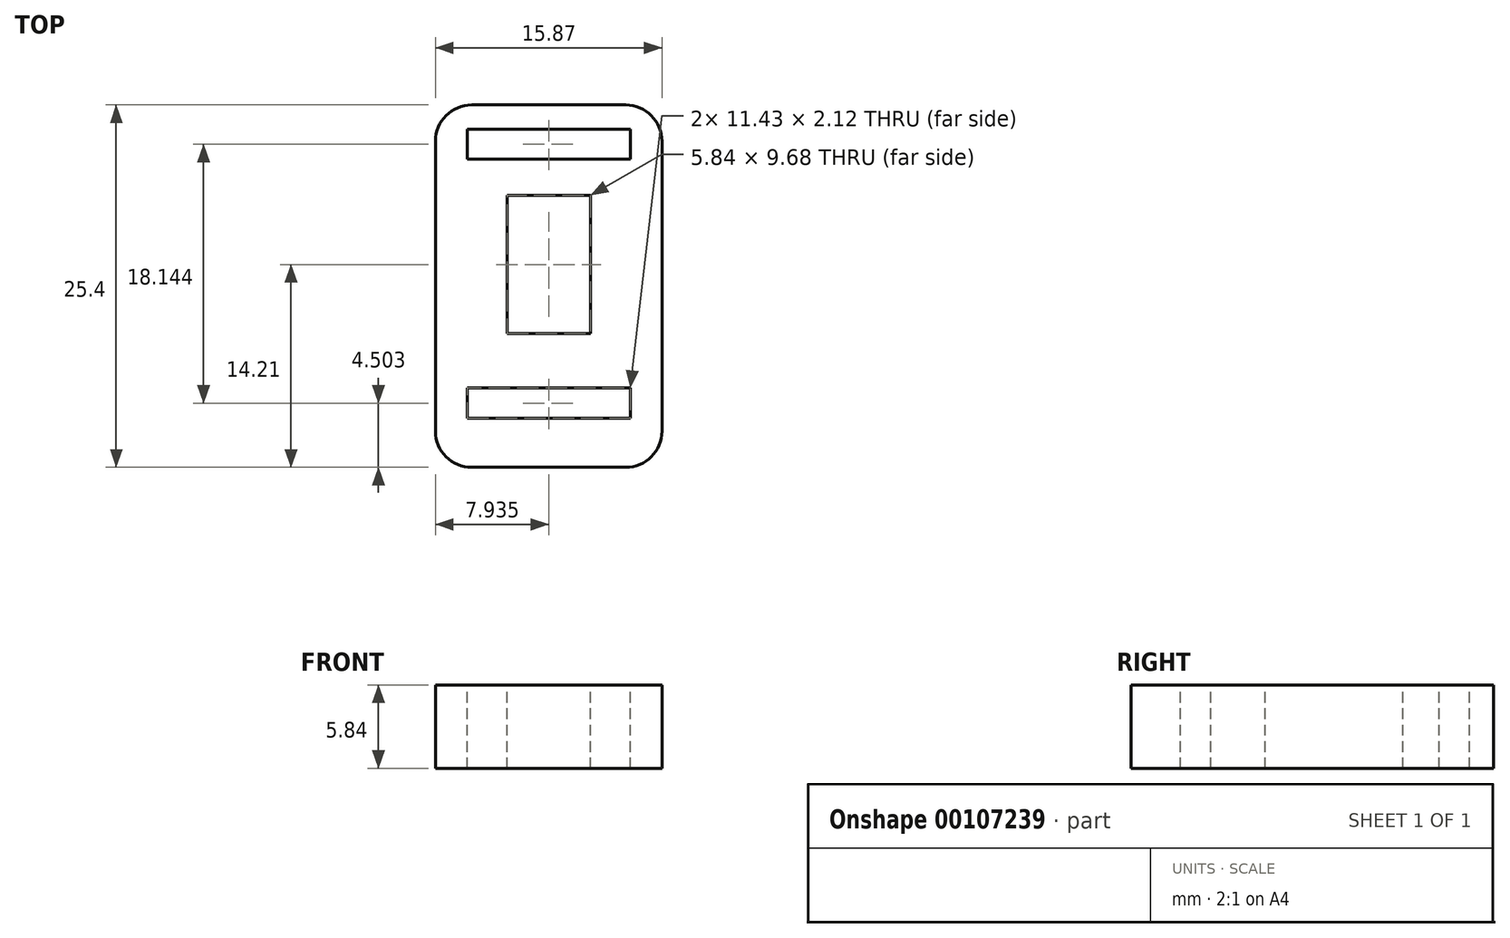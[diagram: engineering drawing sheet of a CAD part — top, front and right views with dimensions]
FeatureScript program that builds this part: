
annotation { "Feature Type Name" : "Feature", "Feature Type Description" : "" }
export const myFeature = defineFeature(function(context is Context, id is Id, definition is map)
    precondition{}
    {
        {
            var Q0;
            Q0=qCreatedBy(makeId("Top.planeOp"),FACE);
            var sketch = newSketch(context, id + "F0", { "sketchPlane" : qUnion([Q0])});
            skLineSegment(sketch, "E0.bottom", {"start": v(-6.16, -11.37) * mm, "end": v(4.63, -11.37) * mm});
            skLineSegment(sketch, "E0.top", {"start": v(-6.16, -36.77) * mm, "end": v(4.63, -36.77) * mm});
            skLineSegment(sketch, "E0.left", {"start": v(-8.7, -13.91) * mm, "end": v(-8.7, -34.23) * mm});
            skLineSegment(sketch, "E0.right", {"start": v(7.17, -13.91) * mm, "end": v(7.17, -34.23) * mm});
            skPoint(sketch, "E1", {"position": v(-0.76, -11.37) * mm});
            skPoint(sketch, "E2.visualSharp", {"position": v(-8.7, -11.37) * mm});
            skArc(sketch, "E2.filletArc", {"start": v(-6.16, -11.37) * mm, "mid": v(-7.96, -12.12) * mm, "end": v(-8.7, -13.91) * mm});
            skPoint(sketch, "E3.visualSharp", {"position": v(7.17, -11.37) * mm});
            skArc(sketch, "E3.filletArc", {"start": v(7.17, -13.91) * mm, "mid": v(6.43, -12.12) * mm, "end": v(4.63, -11.37) * mm});
            skPoint(sketch, "E4.visualSharp", {"position": v(-8.7, -36.77) * mm});
            skArc(sketch, "E4.filletArc", {"start": v(-8.7, -34.23) * mm, "mid": v(-7.96, -36.03) * mm, "end": v(-6.16, -36.77) * mm});
            skPoint(sketch, "E5.visualSharp", {"position": v(7.17, -36.77) * mm});
            skArc(sketch, "E5.filletArc", {"start": v(4.63, -36.77) * mm, "mid": v(6.43, -36.03) * mm, "end": v(7.17, -34.23) * mm});
            skSolve(sketch);
        }
        {
            var Q0;
            Q0=makeQuery(id+"F0.imprint","IMPRINT",FACE,{"disambiguationData":[TD([[makeQuery(id+"F0.imprint","IMPRINT",EDGE,{"derivedFrom":sQuery(id+"F0.wireOp",EDGE,"E0.bottom")}),-1.0]])]});
            extrude(context, id + "F1", {"entities" : qUnion([Q0]), "oppositeDirection" : true, "depth" : 5.84 * mm});
        }
        {
            var Q0;
            Q0=qCreatedBy(makeId("Top.planeOp"),FACE);
            var sketch = newSketch(context, id + "F2", { "sketchPlane" : qUnion([Q0])});
            skLineSegment(sketch, "E6.bottom", {"start": v(-3.69, -17.72) * mm, "end": v(2.16, -17.72) * mm});
            skLineSegment(sketch, "E6.top", {"start": v(-3.69, -27.4) * mm, "end": v(2.16, -27.4) * mm});
            skLineSegment(sketch, "E6.left", {"start": v(-3.69, -17.72) * mm, "end": v(-3.69, -27.4) * mm});
            skLineSegment(sketch, "E6.right", {"start": v(2.16, -17.72) * mm, "end": v(2.16, -27.4) * mm});
            skPoint(sketch, "E7", {"position": v(-0.76, -17.72) * mm});
            skLineSegment(sketch, "E8.bottom", {"start": v(-6.48, -31.2) * mm, "end": v(4.95, -31.2) * mm});
            skLineSegment(sketch, "E8.top", {"start": v(-6.48, -33.33) * mm, "end": v(4.95, -33.33) * mm});
            skLineSegment(sketch, "E8.left", {"start": v(-6.48, -31.2) * mm, "end": v(-6.48, -33.33) * mm});
            skLineSegment(sketch, "E8.right", {"start": v(4.95, -31.2) * mm, "end": v(4.95, -33.33) * mm});
            skPoint(sketch, "E9", {"position": v(-0.76, -31.2) * mm});
            skLineSegment(sketch, "E10.bottom", {"start": v(-6.48, -15.18) * mm, "end": v(4.95, -15.18) * mm});
            skLineSegment(sketch, "E10.top", {"start": v(-6.48, -13.07) * mm, "end": v(4.95, -13.07) * mm});
            skLineSegment(sketch, "E10.left", {"start": v(-6.48, -15.18) * mm, "end": v(-6.48, -13.07) * mm});
            skLineSegment(sketch, "E10.right", {"start": v(4.95, -15.18) * mm, "end": v(4.95, -13.07) * mm});
            skPoint(sketch, "E11", {"position": v(-0.76, -13.07) * mm});
            skSolve(sketch);
        }
        {
            var Q0;
            Q0=makeQuery(id+"F2.imprint","IMPRINT",FACE,{"disambiguationData":[TD([[makeQuery(id+"F2.imprint","IMPRINT",EDGE,{"derivedFrom":sQuery(id+"F2.wireOp",EDGE,"E6.bottom")}),-1.0]])]});
            var Q1;
            Q1=makeQuery(id+"F2.imprint","IMPRINT",FACE,{"disambiguationData":[TD([[makeQuery(id+"F2.imprint","IMPRINT",EDGE,{"derivedFrom":sQuery(id+"F2.wireOp",EDGE,"E8.bottom")}),-1.0]])]});
            var Q2;
            Q2=makeQuery(id+"F2.imprint","IMPRINT",FACE,{"disambiguationData":[TD([[makeQuery(id+"F2.imprint","IMPRINT",EDGE,{"derivedFrom":sQuery(id+"F2.wireOp",EDGE,"E10.bottom")}),1.0]])]});
            var Q3;
            Q3=makeQuery(id+"F1.opExtrude","CAP_FACE",FACE,{"disambiguationData":[OSD([sQuery(id+"F0.wireOp",EDGE,"E0.bottom"),sQuery(id+"F0.wireOp",EDGE,"E0.top"),sQuery(id+"F0.wireOp",EDGE,"E0.left"),sQuery(id+"F0.wireOp",EDGE,"E0.right")])],"isStart":false});
            extrude(context, id + "F3", {"entities" : qUnion([Q0, Q1, Q2]), "operationType" : NewBodyOperationType.REMOVE, "endBound" : BoundingType.UP_TO_SURFACE, "oppositeDirection" : true, "endBoundEntityFace" : qUnion([Q3]), "depth" : 25.4 * mm});
        }
    });
